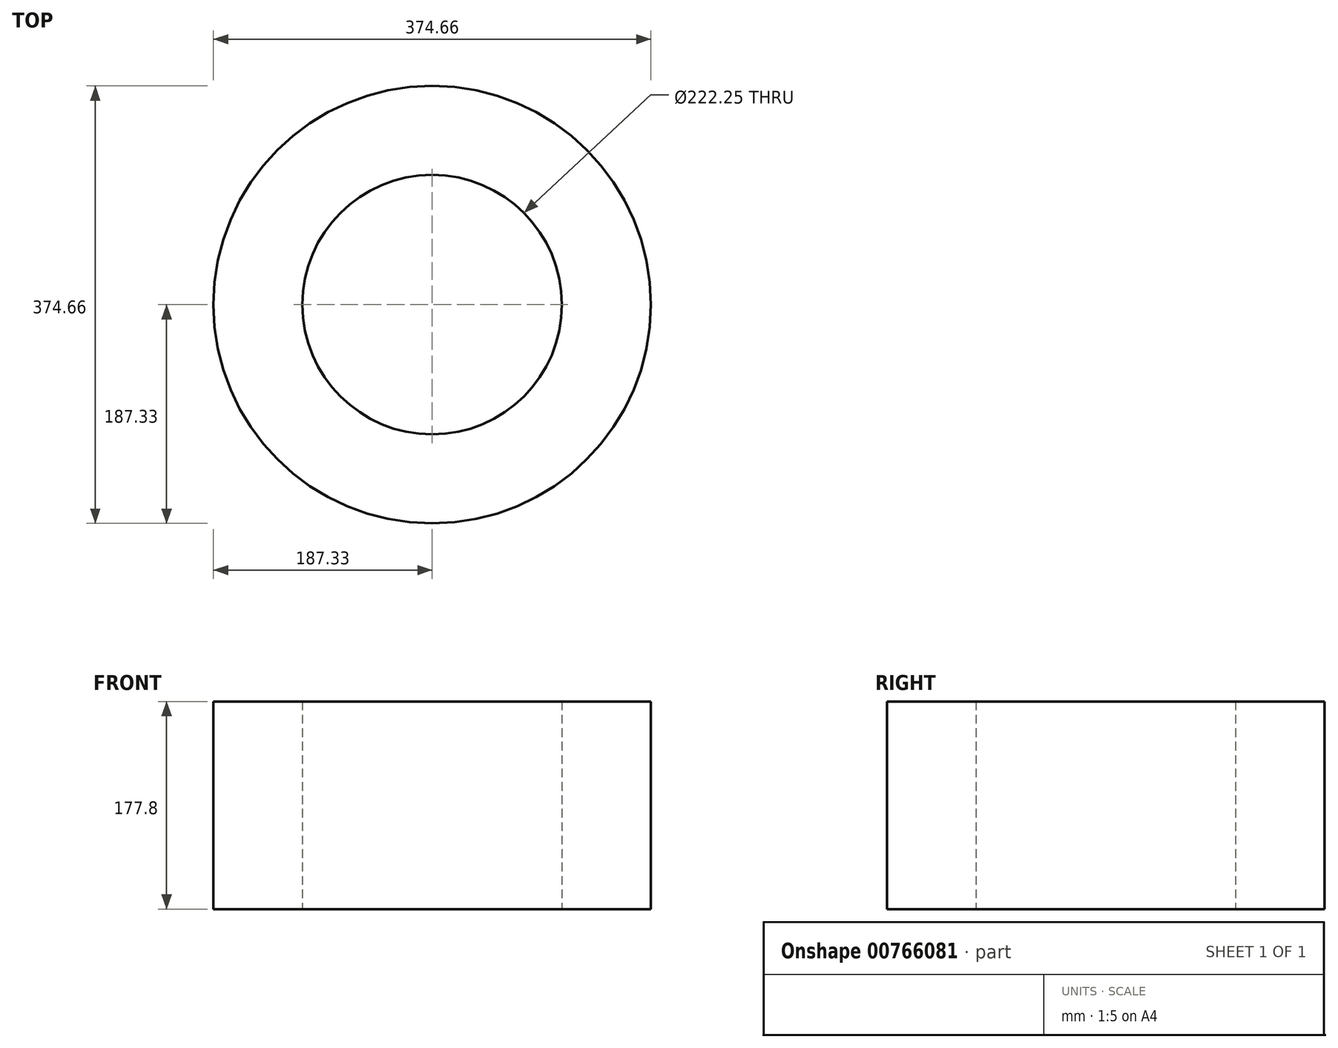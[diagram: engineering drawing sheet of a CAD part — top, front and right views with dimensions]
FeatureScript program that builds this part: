
annotation { "Feature Type Name" : "Feature", "Feature Type Description" : "" }
export const myFeature = defineFeature(function(context is Context, id is Id, definition is map)
    precondition{}
    {
        {
            var Q0;
            Q0=qCreatedBy(makeId("Front.planeOp"),FACE);
            var sketch = newSketch(context, id + "F0", { "sketchPlane" : qUnion([Q0])});
            skLineSegment(sketch, "E0", {"start": v(0, 0) * mm, "end": v(0, 719.83) * mm, "construction": true});
            skLineSegment(sketch, "E1", {"start": v(381, 727.2) * mm, "end": v(381, -112.59) * mm, "construction": true});
            skLineSegment(sketch, "E2", {"start": v(-124.84, 645.16) * mm, "end": v(765.44, 645.16) * mm});
            skLineSegment(sketch, "E3", {"start": v(114.3, -53.81) * mm, "end": v(114.3, 714.98) * mm, "construction": true});
            skLineSegment(sketch, "E4", {"start": v(120.65, 406.95) * mm, "end": v(120.65, 550.02) * mm, "construction": true});
            skLineSegment(sketch, "E5", {"start": v(111.12, 330.2) * mm, "end": v(111.13, 0) * mm});
            skLineSegment(sketch, "E6", {"start": v(-153.27, 304.8) * mm, "end": v(640.71, 304.8) * mm, "construction": true});
            skLineSegment(sketch, "E7", {"start": v(111.13, 0) * mm, "end": v(330.2, 0) * mm});
            skLineSegment(sketch, "E8", {"start": v(136.53, 330.2) * mm, "end": v(136.53, 609.6) * mm});
            skLineSegment(sketch, "E9", {"start": v(136.53, 609.6) * mm, "end": v(355.6, 609.6) * mm});
            skLineSegment(sketch, "E10", {"start": v(355.6, 609.6) * mm, "end": v(355.6, 279.4) * mm});
            skLineSegment(sketch, "E11", {"start": v(355.6, 279.4) * mm, "end": v(330.2, 279.4) * mm});
            skLineSegment(sketch, "E12", {"start": v(330.2, 279.4) * mm, "end": v(330.2, 0) * mm});
            skLineSegment(sketch, "E13", {"start": v(111.13, 330.2) * mm, "end": v(136.53, 330.2) * mm});
            skLineSegment(sketch, "E14", {"start": v(111.13, 177.8) * mm, "end": v(187.33, 177.8) * mm});
            skLineSegment(sketch, "E15", {"start": v(187.33, 177.8) * mm, "end": v(187.33, 0) * mm});
            skLineSegment(sketch, "E16", {"start": v(279.4, 609.6) * mm, "end": v(279.4, 431.8) * mm});
            skLineSegment(sketch, "E17", {"start": v(279.4, 431.8) * mm, "end": v(355.6, 431.8) * mm});
            skSolve(sketch);
        }
        {
            var Q0;
            Q0=makeQuery(id+"F0.imprint","IMPRINT",FACE,{"disambiguationData":[TD([[makeQuery(id+"F0.imprint","IMPRINT",EDGE,{"derivedFrom":sQuery(id+"F0.wireOp",EDGE,"E5")}),1.0]])]});
            var Q1;
            Q1=sQuery(id+"F0.wireOp",EDGE,"E0");
            revolve(context, id + "F1", {"surfaceOperationType" : NewSurfaceOperationType.NEW, "entities" : qUnion([Q0]), "axis" : qUnion([Q1]), "revolveType" : RevolveType.FULL});
        }
    });
